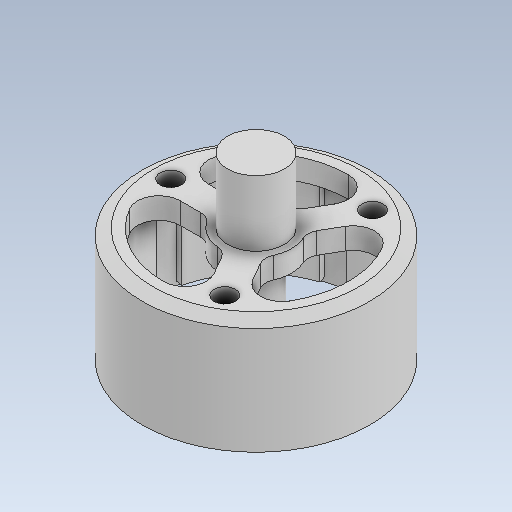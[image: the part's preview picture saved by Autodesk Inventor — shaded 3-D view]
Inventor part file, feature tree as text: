
AUTODESK INVENTOR PART (.ipt)
format: ipt  version: 2020 (Build 240168000, 168)  size: 329,216 bytes
history: native  units: mm
features: extrude x7, sketch x7, pattern_circular x5, projected_geometry x5, fillet x2, chamfer x1
ambient origin geometry x8: Origin, YZ Plane, XZ Plane, XY Plane, X Axis, Y Axis, Z Axis, Center Point
bodies: Solid1 (feature_tree)
feature tree (27):
  extrude  "Extrusion1"  Depth=8.0mm TaperAngle=0.0deg
  extrude  "Extrusion2"  Depth=4.6mm TaperAngle=0.0deg
  extrude  "Extrusion3"  Depth=6.5mm TaperAngle=0.0deg
  extrude  "Extrusion4"  Depth=4.014257mm
  pattern_circular  "Circular Pattern1"  Count=10 Angle=360.0deg
  extrude  "Extrusion5"  Depth=5.0mm
  pattern_circular  "Circular Pattern2"  Count=2  [1 undecoded]
  fillet  "Fillet1"  [1 undecoded]
  pattern_circular  "Circular Pattern3"  [2 undecoded]
  fillet  "Fillet2"  Radius=20.0mm
  pattern_circular  "Circular Pattern4"  [2 undecoded]
  chamfer  "Chamfer1"  Distance=30.0mm Angle=360.0deg
  extrude  "Extrusion6"  Depth=1.5mm
  extrude  "Extrusion7"  Depth=1.0mm TaperAngle=360.0deg
  pattern_circular  "Circular Pattern5"  [2 undecoded]
  sketch  "Sketch1"  dims[d0=16.0mm d1=8.0mm d2=0.0mm]
  sketch  "Sketch2"  dims[d3=4.0mm d4=4.6mm d5=0.0mm]
  projected_geometry  "Projected Loop1"
  sketch  "Sketch3"  dims[d6=15.0mm d7=6.5mm d8=0.0mm]
  projected_geometry  "Projected Loop2"
  sketch  "Sketch4"  dims[d9=14.0mm d10=4.014257mm]
  projected_geometry  "Projected Loop3"
  sketch  "Sketch5"  dims[d11=6.2mm d12=0.0mm d13=100.0mm d14=360.0deg]
  sketch  "Sketch6"  dims[d16=5.0mm d17=13.0mm]
  projected_geometry  "Projected Loop4"
  sketch  "Sketch7"  dims[d18=2.0mm d19=20.0mm d20=120.0deg d21=2.0mm d22=20.0mm d23=6.2mm d24=0.0mm d25=30.0mm d26=360.0deg d28=1.5mm d29=30.0mm d30=360.0deg d32=1.0mm d33=30.0mm d34=360.0deg d36=0.8mm d37=2.0mm d38=30.0deg d39=3.0mm d40=5.0mm d41=0.0mm d42=6.0mm d43=1.5mm d44=5.0mm d45=0.0mm d46=30.0mm d47=360.0deg]
  projected_geometry  "Projected Loop5"
note: 8 required parameter values undecoded (feature->parameter linkage not recoverable at this tier; creation-order binding heuristic only, values carry confidence <= 0.55)
